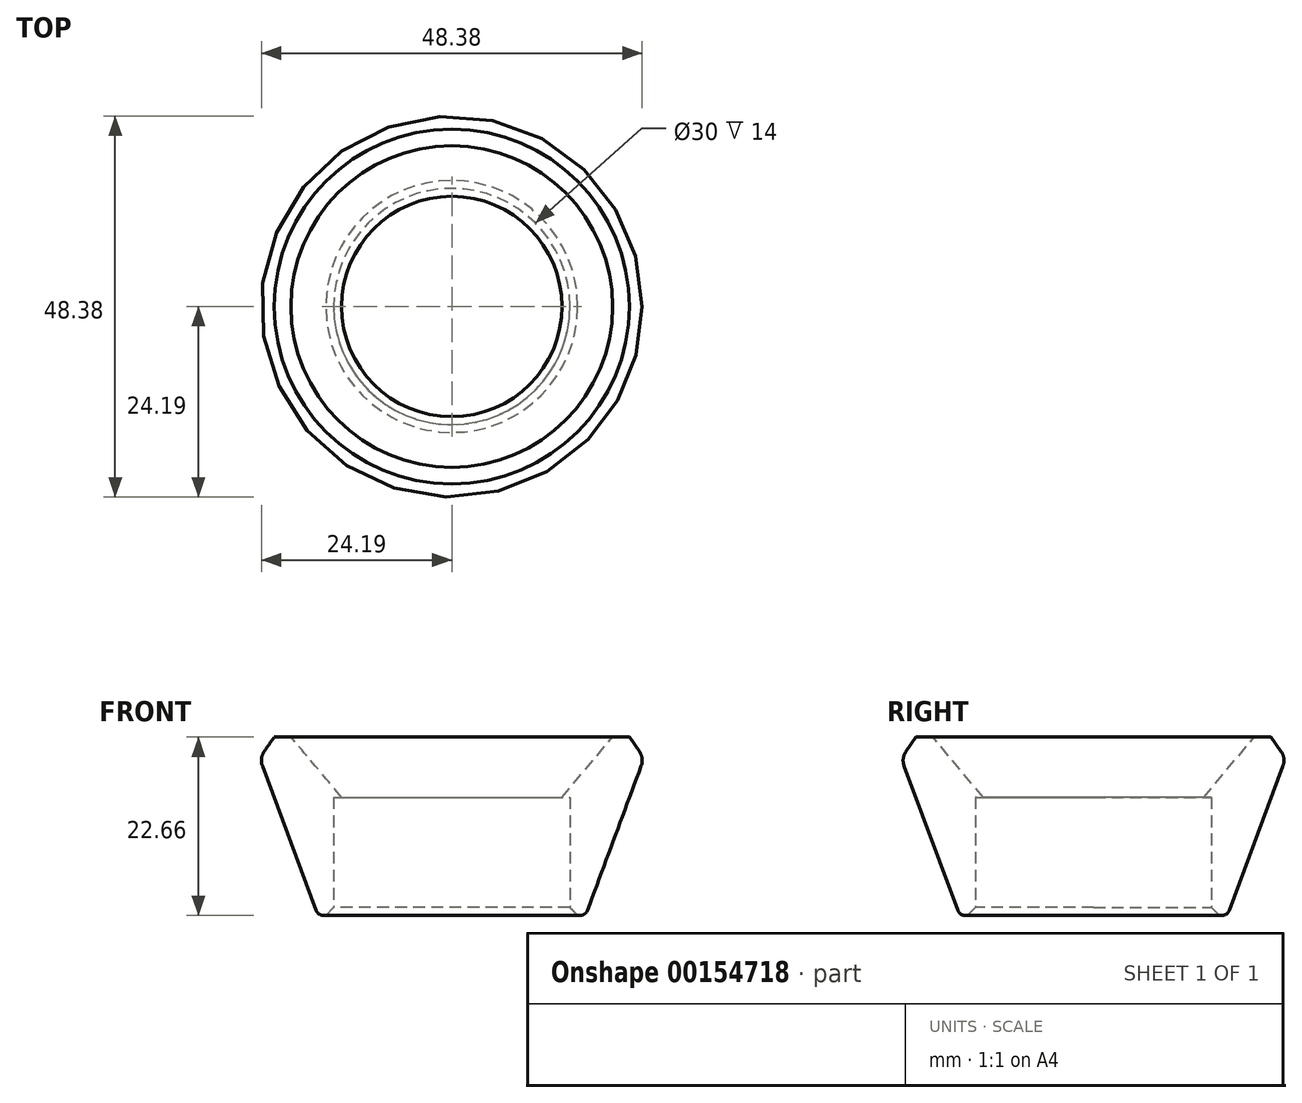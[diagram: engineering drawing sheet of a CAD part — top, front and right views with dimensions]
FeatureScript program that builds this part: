
annotation { "Feature Type Name" : "Feature", "Feature Type Description" : "" }
export const myFeature = defineFeature(function(context is Context, id is Id, definition is map)
    precondition{}
    {
        {
            var Q0;
            Q0=qCreatedBy(makeId("Front.planeOp"),FACE);
            var sketch = newSketch(context, id + "F0", { "sketchPlane" : qUnion([Q0])});
            skLineSegment(sketch, "E0", {"start": v(0, 0) * mm, "end": v(0, 15) * mm, "construction": true});
            skLineSegment(sketch, "E1", {"start": v(0, 0) * mm, "end": v(15, 0) * mm, "construction": true});
            skLineSegment(sketch, "E2", {"start": v(15, 0) * mm, "end": v(15, 15) * mm});
            skLineSegment(sketch, "E3", {"start": v(15, 15) * mm, "end": v(14, 15) * mm});
            skLineSegment(sketch, "E4", {"start": v(14, 15) * mm, "end": v(20.43, 22.66) * mm});
            skLineSegment(sketch, "E5", {"start": v(20.43, 22.66) * mm, "end": v(25.43, 22.66) * mm});
            skLineSegment(sketch, "E6", {"start": v(17, 0) * mm, "end": v(15, 0) * mm});
            skLineSegment(sketch, "E7", {"start": v(17, 0) * mm, "end": v(25.43, 22.66) * mm});
            skLineSegment(sketch, "E8", {"start": v(0, 15) * mm, "end": v(14, 15) * mm, "construction": true});
            skSolve(sketch);
        }
        {
            var Q0;
            Q0=makeQuery(id+"F0.imprint","IMPRINT",FACE,{"disambiguationData":[TD([[makeQuery(id+"F0.imprint","IMPRINT",EDGE,{"derivedFrom":sQuery(id+"F0.wireOp",EDGE,"E2")}),-1.0]])]});
            var Q1;
            Q1=sQuery(id+"F0.wireOp",EDGE,"E0");
            revolve(context, id + "F1", {"entities" : qUnion([Q0]), "axis" : qUnion([Q1]), "revolveType" : RevolveType.FULL});
        }
        {
            var Q0;
            Q0=makeQuery(id+"F1.opRevolve","SWEPT_EDGE",EDGE,{"disambiguationData":[OSD([sQuery(id+"F0.wireOp",EDGE,"E5"),sQuery(id+"F0.wireOp",EDGE,"E7")])]});
            chamfer(context, id + "F2", {"entities" : qUnion([Q0]), "width" : 2 * mm, "tangentPropagation" : true});
        }
        {
            var Q0;
            {var subQ0=sQuery(id+"F0.wireOp",EDGE,"E7");Q0=makeQuery(id+"F2.opChamfer","BLEND_EDGE",EDGE,{"blendedFrom":[makeQuery(id+"F1.opRevolve","SWEPT_EDGE",EDGE,{"disambiguationData":[OSD([sQuery(id+"F0.wireOp",EDGE,"E5"),subQ0])]}),makeQuery(id+"F1.opRevolve","SWEPT_FACE",FACE,{"disambiguationData":[OSD([subQ0])]})],"blendedInto":[makeQuery(id+"F1.opRevolve","SWEPT_FACE",FACE,{"disambiguationData":[OSD([subQ0])]})]});}
            fillet(context, id + "F3", {"entities" : qUnion([Q0]), "radius" : 2 * mm, "tangentPropagation" : true, "allowEdgeOverflow" : false});
        }
        {
            var Q0;
            Q0=makeQuery(id+"F1.opRevolve","SWEPT_EDGE",EDGE,{"disambiguationData":[OSD([sQuery(id+"F0.wireOp",EDGE,"E2"),sQuery(id+"F0.wireOp",EDGE,"E6")])]});
            chamfer(context, id + "F4", {"entities" : qUnion([Q0]), "width" : 1 * mm, "tangentPropagation" : true});
        }
        {
            var Q0;
            Q0=makeQuery(id+"F1.opRevolve","SWEPT_EDGE",EDGE,{"disambiguationData":[OSD([sQuery(id+"F0.wireOp",EDGE,"E6"),sQuery(id+"F0.wireOp",EDGE,"E7")])]});
            fillet(context, id + "F5", {"entities" : qUnion([Q0]), "radius" : 1 * mm, "tangentPropagation" : true, "allowEdgeOverflow" : false});
        }
    });
